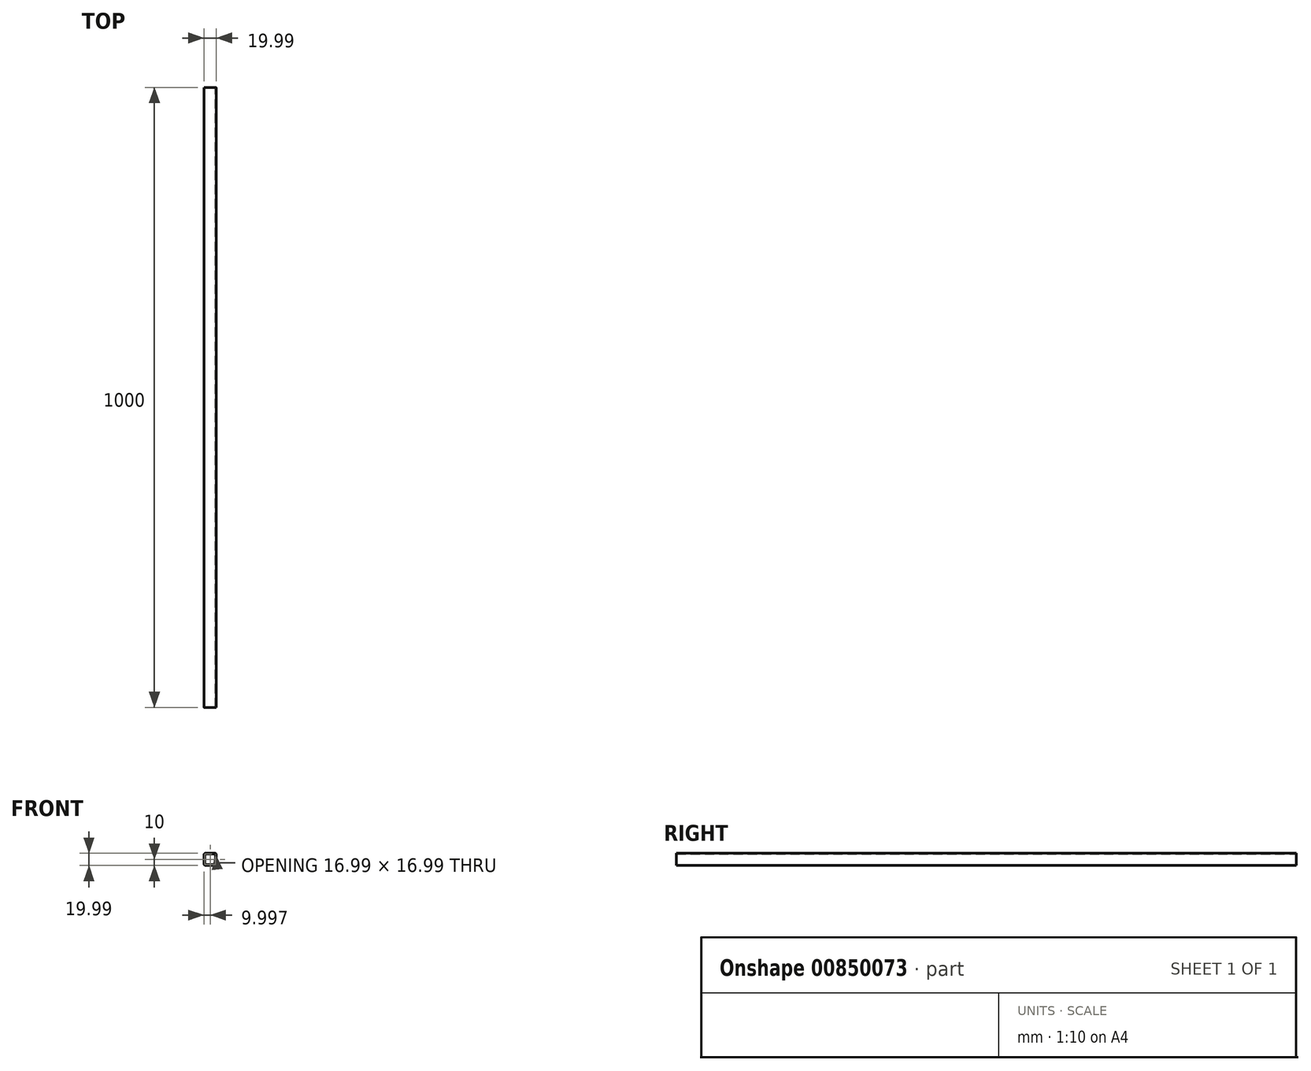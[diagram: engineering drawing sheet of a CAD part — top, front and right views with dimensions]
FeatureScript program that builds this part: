
annotation { "Feature Type Name" : "Feature", "Feature Type Description" : "" }
export const myFeature = defineFeature(function(context is Context, id is Id, definition is map)
    precondition{}
    {
        {
            var Q0;
            Q0=qCreatedBy(makeId("Front.planeOp"),FACE);
            var sketch = newSketch(context, id + "F0", { "sketchPlane" : qUnion([Q0])});
            skLineSegment(sketch, "E0.bottom", {"start": v(-0.29, -10.23) * mm, "end": v(-14.74, -10.23) * mm});
            skLineSegment(sketch, "E0.top", {"start": v(-0.29, 6.77) * mm, "end": v(-14.74, 6.77) * mm});
            skLineSegment(sketch, "E0.left", {"start": v(0.98, -8.96) * mm, "end": v(0.98, 5.5) * mm});
            skLineSegment(sketch, "E0.right", {"start": v(-16, -8.96) * mm, "end": v(-16, 5.5) * mm});
            skPoint(sketch, "E1.visualSharp", {"position": v(-16, 6.77) * mm});
            skArc(sketch, "E1.filletArc", {"start": v(-14.74, 6.77) * mm, "mid": v(-15.64, 6.4) * mm, "end": v(-16, 5.5) * mm});
            skPoint(sketch, "E2.visualSharp", {"position": v(-16, -10.23) * mm});
            skArc(sketch, "E2.filletArc", {"start": v(-16, -8.96) * mm, "mid": v(-15.64, -9.85) * mm, "end": v(-14.74, -10.23) * mm});
            skPoint(sketch, "E3.visualSharp", {"position": v(0.98, -10.23) * mm});
            skArc(sketch, "E3.filletArc", {"start": v(-0.29, -10.23) * mm, "mid": v(0.61, -9.85) * mm, "end": v(0.98, -8.96) * mm});
            skPoint(sketch, "E4.visualSharp", {"position": v(0.98, 6.77) * mm});
            skArc(sketch, "E4.filletArc", {"start": v(0.98, 5.5) * mm, "mid": v(0.61, 6.4) * mm, "end": v(-0.29, 6.77) * mm});
            skArc(sketch, "E5.0", {"start": v(-0.29, -11.73) * mm, "mid": v(1.67, -10.91) * mm, "end": v(2.48, -8.96) * mm});
            skLineSegment(sketch, "E5.1", {"start": v(-0.29, -11.73) * mm, "end": v(-14.74, -11.73) * mm});
            skLineSegment(sketch, "E5.2", {"start": v(2.48, -8.96) * mm, "end": v(2.48, 5.5) * mm});
            skArc(sketch, "E5.3", {"start": v(-17.5, -8.96) * mm, "mid": v(-16.7, -10.91) * mm, "end": v(-14.74, -11.73) * mm});
            skArc(sketch, "E5.4", {"start": v(2.48, 5.5) * mm, "mid": v(1.67, 7.45) * mm, "end": v(-0.29, 8.26) * mm});
            skLineSegment(sketch, "E5.5", {"start": v(-0.29, 8.26) * mm, "end": v(-14.74, 8.26) * mm});
            skArc(sketch, "E5.6", {"start": v(-14.74, 8.26) * mm, "mid": v(-16.7, 7.45) * mm, "end": v(-17.5, 5.5) * mm});
            skLineSegment(sketch, "E5.7", {"start": v(-17.5, -8.96) * mm, "end": v(-17.5, 5.5) * mm});
            skSolve(sketch);
        }
        {
            var Q0;
            Q0=makeQuery(id+"F0.imprint","IMPRINT",FACE,{"disambiguationData":[TD([[makeQuery(id+"F0.imprint","IMPRINT",EDGE,{"derivedFrom":sQuery(id+"F0.wireOp",EDGE,"E0.bottom")}),1.0]])]});
            extrude(context, id + "F1", {"entities" : qUnion([Q0]), "depth" : 1000 * mm, "offsetDistance" : 25.4 * mm});
        }
    });
